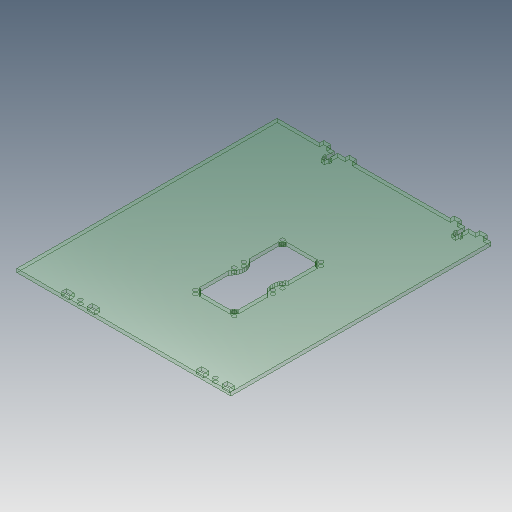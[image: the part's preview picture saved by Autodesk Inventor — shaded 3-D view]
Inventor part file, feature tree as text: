
AUTODESK INVENTOR PART (.ipt)
format: ipt  version: 2017 (Build 210142000, 142)  size: 784,896 bytes
history: native  units: mm
features: extrude x1, hole x1, sketch x1, projected_geometry x1
ambient origin geometry x8: Origin, YZ Plane, XZ Plane, XY Plane, X Axis, Y Axis, Z Axis, Center Point
bodies: Solid1 (feature_tree)
feature tree (4):
  extrude  "Extrusion1"  [1 undecoded]
  hole  "Hole1"  [1 undecoded]
  sketch  "Sketch2"  dims[d0=3.0mm d1=0.0mm d2=3.4mm d3=6.0mm d4=4.0mm d5=2.0mm d6=90.0deg d7=8.0mm d8=20.594885mm]
  projected_geometry  "Projected Loop1"
note: 2 required parameter values undecoded (feature->parameter linkage not recoverable at this tier; creation-order binding heuristic only, values carry confidence <= 0.55)
